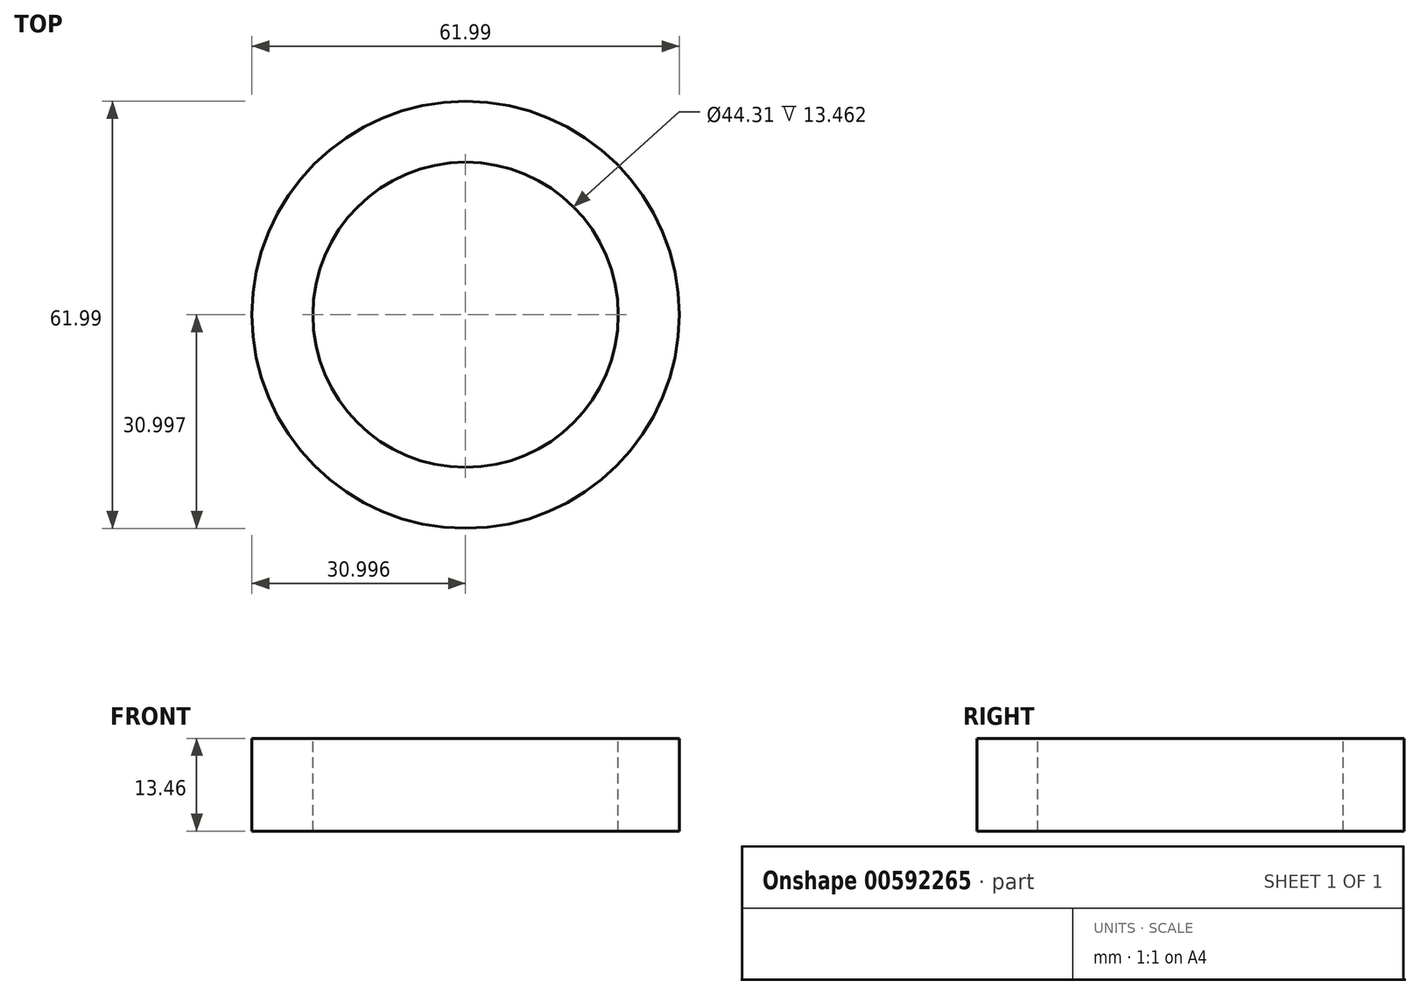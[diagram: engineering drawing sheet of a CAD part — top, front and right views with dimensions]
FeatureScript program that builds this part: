
annotation { "Feature Type Name" : "Feature", "Feature Type Description" : "" }
export const myFeature = defineFeature(function(context is Context, id is Id, definition is map)
    precondition{}
    {
        {
            var Q0;
            Q0=qCreatedBy(makeId("Top.planeOp"),FACE);
            var sketch = newSketch(context, id + "F0", { "sketchPlane" : qUnion([Q0])});
            skCircle(sketch, "E0", {"center": v(-25.86, -26.34) * mm, "radius": 31 * mm});
            skCircle(sketch, "E1", {"center": v(-25.86, -26.34) * mm, "radius": 22.15 * mm});
            skSolve(sketch);
        }
        {
            var Q0;
            Q0=makeQuery(id+"F0.imprint","IMPRINT",FACE,{"disambiguationData":[TD([[makeQuery(id+"F0.imprint","IMPRINT",EDGE,{"derivedFrom":sQuery(id+"F0.wireOp",EDGE,"E0")}),1.0]])]});
            extrude(context, id + "F1", {"entities" : qUnion([Q0]), "oppositeDirection" : true, "depth" : 13.46 * mm, "offsetDistance" : 25.4 * mm});
        }
    });
